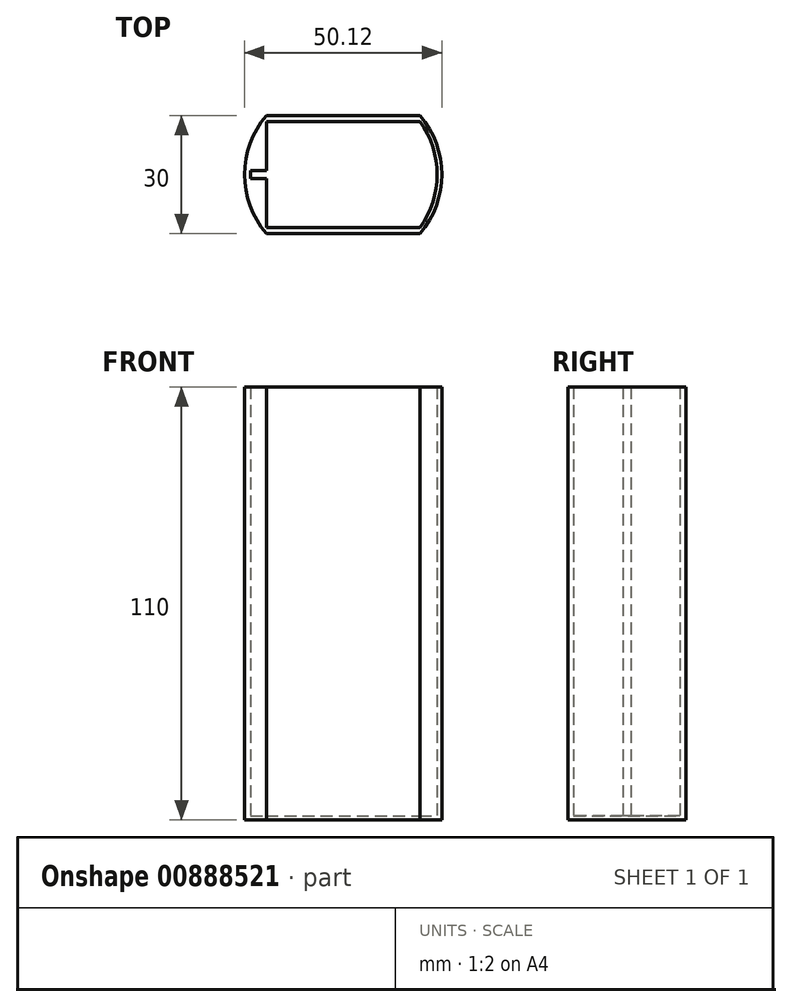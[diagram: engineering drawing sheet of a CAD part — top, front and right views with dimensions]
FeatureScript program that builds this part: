
annotation { "Feature Type Name" : "Feature", "Feature Type Description" : "" }
export const myFeature = defineFeature(function(context is Context, id is Id, definition is map)
    precondition{}
    {
        {
            var Q0;
            Q0=qCreatedBy(makeId("Top.planeOp"),FACE);
            var sketch = newSketch(context, id + "F0", { "sketchPlane" : qUnion([Q0])});
            skLineSegment(sketch, "E0", {"start": v(-22.5, 32.04) * mm, "end": v(16.5, 32.04) * mm});
            skLineSegment(sketch, "E1", {"start": v(-22.5, 2.04) * mm, "end": v(16.5, 2.04) * mm});
            skArc(sketch, "E2", {"start": v(-22.5, 32.04) * mm, "mid": v(-28.06, 17.04) * mm, "end": v(-22.5, 2.04) * mm});
            skArc(sketch, "E3", {"start": v(16.5, 2.04) * mm, "mid": v(22.06, 17.04) * mm, "end": v(16.5, 32.04) * mm});
            skSolve(sketch);
        }
        {
            var Q0;
            Q0 = qSketchRegion(id + "F0", true);
            extrude(context, id + "F1", {"entities" : qUnion([Q0]), "depth" : 1 * mm, "offsetDistance" : 25 * mm});
        }
        {
            var Q0;
            Q0=makeQuery(id+"F1.opExtrude","CAP_FACE",FACE,{"disambiguationData":[OSD([sQuery(id+"F0.wireOp",EDGE,"E0"),sQuery(id+"F0.wireOp",EDGE,"E1"),sQuery(id+"F0.wireOp",EDGE,"E2"),sQuery(id+"F0.wireOp",EDGE,"E3")])],"isStart":false});
            var sketch = newSketch(context, id + "F2", { "sketchPlane" : qUnion([Q0])});
            skLineSegment(sketch, "E4", {"start": v(16.5, 32.04) * mm, "end": v(-22.5, 32.04) * mm});
            skLineSegment(sketch, "E5", {"start": v(-22.5, 2.04) * mm, "end": v(16.5, 2.04) * mm});
            skArc(sketch, "E6", {"start": v(-22.5, 32.04) * mm, "mid": v(-28.06, 17.04) * mm, "end": v(-22.5, 2.04) * mm});
            skArc(sketch, "E7", {"start": v(16.5, 2.04) * mm, "mid": v(22.06, 17.04) * mm, "end": v(16.5, 32.04) * mm});
            skLineSegment(sketch, "E8", {"start": v(-22.5, 30.54) * mm, "end": v(16.5, 30.54) * mm});
            skLineSegment(sketch, "E9", {"start": v(-22.5, 3.54) * mm, "end": v(16.5, 3.54) * mm});
            skArc(sketch, "E10", {"start": v(16.5, 3.54) * mm, "mid": v(20.88, 17.04) * mm, "end": v(16.5, 30.54) * mm});
            skLineSegment(sketch, "E11", {"start": v(-22.5, 30.54) * mm, "end": v(-22.5, 18.04) * mm});
            skLineSegment(sketch, "E12", {"start": v(-22.5, 18.04) * mm, "end": v(-26.5, 18.04) * mm});
            skLineSegment(sketch, "E13", {"start": v(-26.5, 18.04) * mm, "end": v(-26.5, 16.04) * mm});
            skLineSegment(sketch, "E14", {"start": v(-26.5, 16.04) * mm, "end": v(-22.5, 16.04) * mm});
            skLineSegment(sketch, "E15", {"start": v(-22.5, 16.04) * mm, "end": v(-22.5, 3.54) * mm});
            skSolve(sketch);
        }
        {
            var Q0;
            Q0=makeQuery(id+"F2.imprint","IMPRINT",FACE,{"disambiguationData":[TD([[makeQuery(id+"F2.imprint","IMPRINT",EDGE,{"derivedFrom":sQuery(id+"F2.wireOp",EDGE,"E4")}),-1.0]])]});
            extrude(context, id + "F3", {"entities" : qUnion([Q0]), "operationType" : NewBodyOperationType.ADD, "depth" : 109 * mm, "offsetDistance" : 25 * mm});
        }
    });
